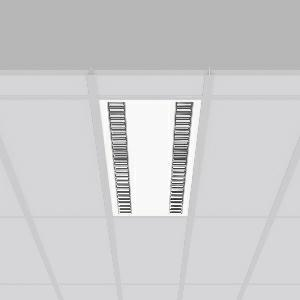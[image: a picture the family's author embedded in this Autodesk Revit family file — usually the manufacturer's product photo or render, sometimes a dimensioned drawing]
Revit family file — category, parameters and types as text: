
# Revit family: sonis_901680_002_1_6861
name_source: partatom
category: Lighting Fixtures
units: mm (PartAtom-declared; Revit-internal decimal feet)

## family parameters
Cut with Voids When Loaded = No
Host = Face
Light Source = No
Part Type = Normal
Room Calculation Point = No
Round Connector Dimension = Use Diameter
Shared = No

## types (1)
- SONIS (1 x LED Modul 840, 6500 lm, 4000)
    Apparent Load = 50 VA
    CIE Flux Codes = 83 100 100 100 100
    Color Rendering = 80
    Color Temperature = 4000
    Default Elevation = 1800 mm
    Description = Series: SONIS
High-efficiency lay-in luminaire for ceiling systems with visible mounting rails. Housing: metal, powder-coated. Alea optical system: Reflector structure (ABS, Aluminium-coated, highly polished) with integrated diffuser made of non-yellowing plastic (PMMA) opal for glare-free light at the workstation. Narrow beam, brilliant luminous effect. Suitable for Recessed ceiling mounting. Driver integrated. Perfect for office areas (RUG < 19) and environments with computer screens in accordance with EN 12464-1. 
Colour: white
Length: 1197 mm
Width: 297 mm
Cut-out length: 1175 mm
Cut-out width: 275 mm
Recess height: 27 mm
Lamp: LED
Socket: without socket
Colour temperature: 4000K
Colour rendering index (CRI): 80
System power: 50 W
Rated luminous flux: 6500 lm
Luminous efficiency: 130 lm/W
Control gear: Regulated power supply
Protection class: I
Type of protection: IP 20
    Height = 0 mm  [stored 0 ft]
    Lamp = 1 x LED Modul 840
    Lamp Light Flux = 6500 lm
    Lamp count = 1
    Length = 1197 mm
    Lifetime = 50000 h
    Luminous efficacy = 130 lm/W
    Manufacturer = RZB
    ModVariant = No
    Model = 901680.002.1
    Mounting Place = Ceiling
    Mounting Type = Recessed
    Number of Poles = 1
    OnlyDefault = Yes
    Power Factor = 1
    Product Name = SONIS
    Product group = Recessed modular luminaires
    ProductGroupID = 406
    Protection Class = Protection class I
    Protection Degree = IP 20
    RLX_Detail_Level = 1
    RLX_Emergency_Light_Flux = 0 lm
    RLX_Emergency_Type = 0
    RLX_Emergency_Type_DB = No
    RlxData = <blob elided: 37021 chars, md5=386ad630>
    Socket = socket
    Standby Power = 0 W
    System Light Flux = 6500 lm
    System Power = 50 W
    Type Comments = Product without accessories
    Type Image = 901648.002.jpg
    URL = http://relux.com
    VarID = ---
    Voltage = 230 V
    Voltage Range = 220-240 V
    Weight = 0.00 kg
    Width = 297 mm

note: [stored X ft] marks values corroborated as IEEE doubles in the binary element streams (Revit-internal decimal feet)

## geometry (parser evidence)
native form markers: Blend x4, Sweep x10
no freeform markers — native parametric forms only
